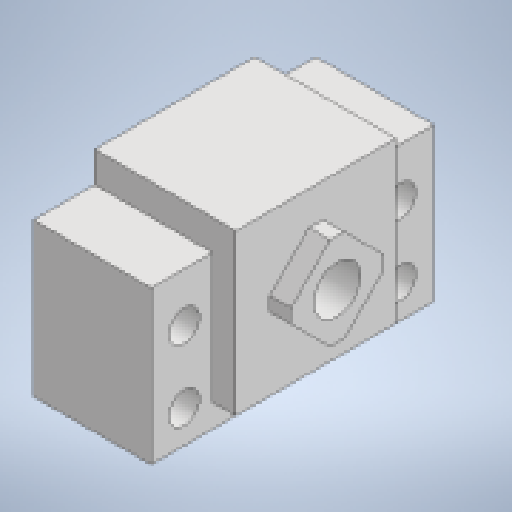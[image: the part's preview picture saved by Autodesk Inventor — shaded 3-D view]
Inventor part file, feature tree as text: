
AUTODESK INVENTOR PART (.ipt)
format: ipt  version: 2023 (Build 270158000, 158)  size: 175,104 bytes
history: native  units: mm
features: extrude x3, sketch x3
ambient origin geometry x8: Origin, YZ Plane, XZ Plane, XY Plane, X Axis, Y Axis, Z Axis, Center Point
bodies: Solid1 (feature_tree)
feature tree (6):
  extrude  "Extrusion1"  Depth=60.0mm
  extrude  "Extrusion2"  Depth=46.0mm
  extrude  "Extrusion3"  Depth=32.5mm
  sketch  "Sketch1"  dims[d0=60.0mm d1=6.6mm]
  sketch  "Sketch2"  dims[d2=15.0mm d3=46.0mm]
  sketch  "Sketch3"  dims[d4=22.0mm d5=32.5mm d6=34.0mm d7=39.0mm d8=10.0mm d9=25.0mm d10=0.0mm d11=5.0mm d12=0.0mm d14=135.0deg d15=16.0mm d16=3.0mm d17=4.5mm d18=0.0mm]
